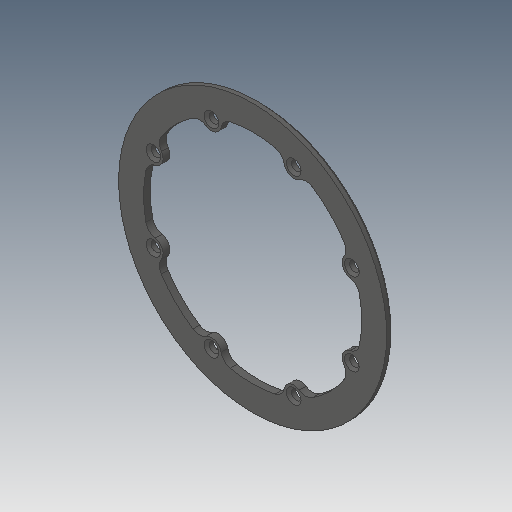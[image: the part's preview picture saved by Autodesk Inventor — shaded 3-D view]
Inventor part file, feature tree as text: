
AUTODESK INVENTOR PART (.ipt)
format: ipt  version: 2019.4 (Build 234330000, 330)  size: 181,248 bytes
history: native  units: mm
features: other x4, sketch x3, reference x3, extrude x2, fillet x1, hole x1, pattern_circular x1, chamfer x1
ambient origin geometry x8: Origin, YZ Plane, XZ Plane, XY Plane, X Axis, Y Axis, Z Axis, Center Point
bodies: Body1 (feature_tree)
feature tree (16):
  other  "ソリッド1"
  extrude  "押し出し1"  Depth=1.0mm TaperAngle=0.0deg
  extrude  "押し出し2"  Depth=1.25mm
  fillet  "フィレット1"  Radius=32.5mm
  hole  "穴2"  [1 undecoded]
  pattern_circular  "円形状パターン1"  [2 undecoded]
  chamfer  "面取り1"  Distance=1.75mm
  sketch  "スケッチ1"
  sketch  "スケッチ2"
  reference  "参照1"
  reference  "参照2"
  reference  "参照3"
  sketch  "スケッチ3"
  parser-record x1  (decoder bookkeeping rows leaked as tree rows — omitted from the tree; the rows remain in map.json)
  other  "COXA_PITCH_DRIVER_PULLEY.iam"
  other  "UPPER_TIMING_PULLEY_P40:1"
note: 3 required parameter values undecoded (feature->parameter linkage not recoverable at this tier; creation-order binding heuristic only, values carry confidence <= 0.55)
note: 1 file-system path scrubbed to <path> (originals preserved in map.json)
